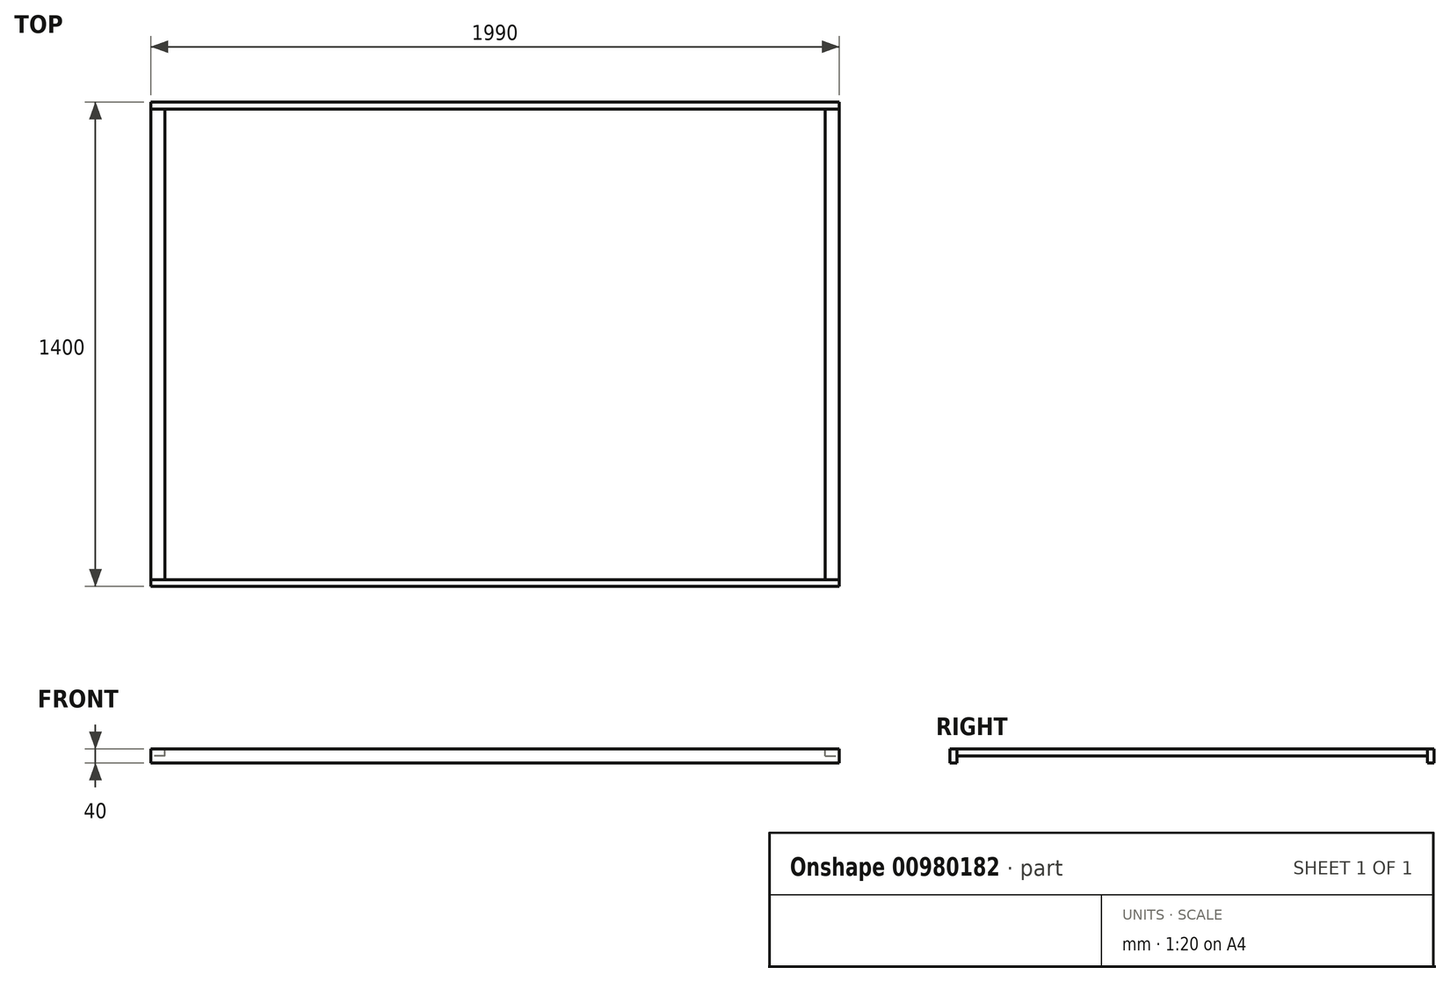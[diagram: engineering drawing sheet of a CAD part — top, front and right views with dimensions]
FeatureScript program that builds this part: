
annotation { "Feature Type Name" : "Feature", "Feature Type Description" : "" }
export const myFeature = defineFeature(function(context is Context, id is Id, definition is map)
    precondition{}
    {
        {
            var Q0;
            Q0=qCreatedBy(makeId("Top.planeOp"),FACE);
            var sketch = newSketch(context, id + "F0", { "sketchPlane" : qUnion([Q0])});
            skLineSegment(sketch, "E0.bottom", {"start": v(995, 700) * mm, "end": v(-995, 700) * mm});
            skLineSegment(sketch, "E0.top", {"start": v(995, -700) * mm, "end": v(-995, -700) * mm});
            skLineSegment(sketch, "E0.left", {"start": v(995, 700) * mm, "end": v(995, -700) * mm});
            skLineSegment(sketch, "E0.right", {"start": v(-995, 700) * mm, "end": v(-995, -700) * mm});
            skPoint(sketch, "E0.middle", {"position": v(0, 0) * mm});
            skLineSegment(sketch, "E1.bottom", {"start": v(955, 680) * mm, "end": v(-955, 680) * mm});
            skLineSegment(sketch, "E1.top", {"start": v(955, -680) * mm, "end": v(-955, -680) * mm});
            skLineSegment(sketch, "E1.left", {"start": v(955, 680) * mm, "end": v(955, -680) * mm});
            skLineSegment(sketch, "E1.right", {"start": v(-955, 680) * mm, "end": v(-955, -680) * mm});
            skLineSegment(sketch, "E2", {"start": v(-955, 680) * mm, "end": v(-995, 680) * mm});
            skLineSegment(sketch, "E3", {"start": v(955, 680) * mm, "end": v(995, 680) * mm});
            skLineSegment(sketch, "E4", {"start": v(955, -680) * mm, "end": v(995, -680) * mm});
            skLineSegment(sketch, "E5", {"start": v(-955, -680) * mm, "end": v(-995, -680) * mm});
            skSolve(sketch);
        }
        {
            var Q0;
            {var subQ1=sQuery(id+"F0.wireOp",EDGE,"E0.bottom");Q0=makeQuery(id+"F0.imprint","IMPRINT",FACE,{"disambiguationData":[TD([[makeQuery(id+"F0.imprint","IMPRINT",EDGE,{"derivedFrom":subQ1}),1.0]])]});}
            var Q1;
            {var subQ1=sQuery(id+"F0.wireOp",EDGE,"E0.top");Q1=makeQuery(id+"F0.imprint","IMPRINT",FACE,{"disambiguationData":[TD([[makeQuery(id+"F0.imprint","IMPRINT",EDGE,{"derivedFrom":subQ1}),-1.0]])]});}
            extrude(context, id + "F1", {"entities" : qUnion([Q0, Q1]), "oppositeDirection" : true, "depth" : 40 * mm, "offsetDistance" : 25 * mm});
        }
        {
            var Q0;
            Q0=makeQuery(id+"F0.imprint","IMPRINT",FACE,{"disambiguationData":[TD([[makeQuery(id+"F0.imprint","IMPRINT",EDGE,{"derivedFrom":sQuery(id+"F0.wireOp",EDGE,"E1.left")}),1.0]])]});
            var Q1;
            Q1=makeQuery(id+"F0.imprint","IMPRINT",FACE,{"disambiguationData":[TD([[makeQuery(id+"F0.imprint","IMPRINT",EDGE,{"derivedFrom":sQuery(id+"F0.wireOp",EDGE,"E1.right")}),-1.0]])]});
            extrude(context, id + "F2", {"entities" : qUnion([Q0, Q1]), "oppositeDirection" : true, "depth" : 20 * mm, "offsetDistance" : 25 * mm});
        }
    });
